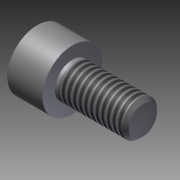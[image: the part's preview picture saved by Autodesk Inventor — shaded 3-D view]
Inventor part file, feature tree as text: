
AUTODESK INVENTOR PART (.ipt)
format: ipt  version: 2013 (Build 170138000, 138)  size: 125,440 bytes
history: native  units: mm
features: other x14, sketch x3, revolve x2, thread x1, extrude x1
ambient origin geometry x8: Origin, YZ Plane, XZ Plane, XY Plane, X Axis, Y Axis, Z Axis, Center Point
bodies: Solid1 (feature_tree)
feature tree (21):
  revolve  "Revolution1"  [1 undecoded]
  thread  "Thread1"  [1 undecoded]
  revolve  "Revolution2"  [1 undecoded]
  extrude  "Extrusion1"  [1 undecoded]
  other  "bolt_XY"
  other  "bolt_YZ"
  other  "bolt_ZX"
  other  "bolt_X"
  other  "bolt_Y"
  other  "bolt_Z"
  other  "bolt_Center"
  other  "nut_XY"
  other  "nut_YZ"
  other  "nut_ZX"
  other  "nut_X"
  other  "nut_Y"
  other  "nut_Z"
  other  "nut_Center"
  sketch  "Sketch_1"  dims[d0=360.0deg d1=9.5mm d2=0.5mm d3=360.0deg]
  sketch  "Sketch_4"
  sketch  "Sketch_3"  dims[d4=2.5mm d5=0.0mm]
note: 4 required parameter values undecoded (feature->parameter linkage not recoverable at this tier; creation-order binding heuristic only, values carry confidence <= 0.55)